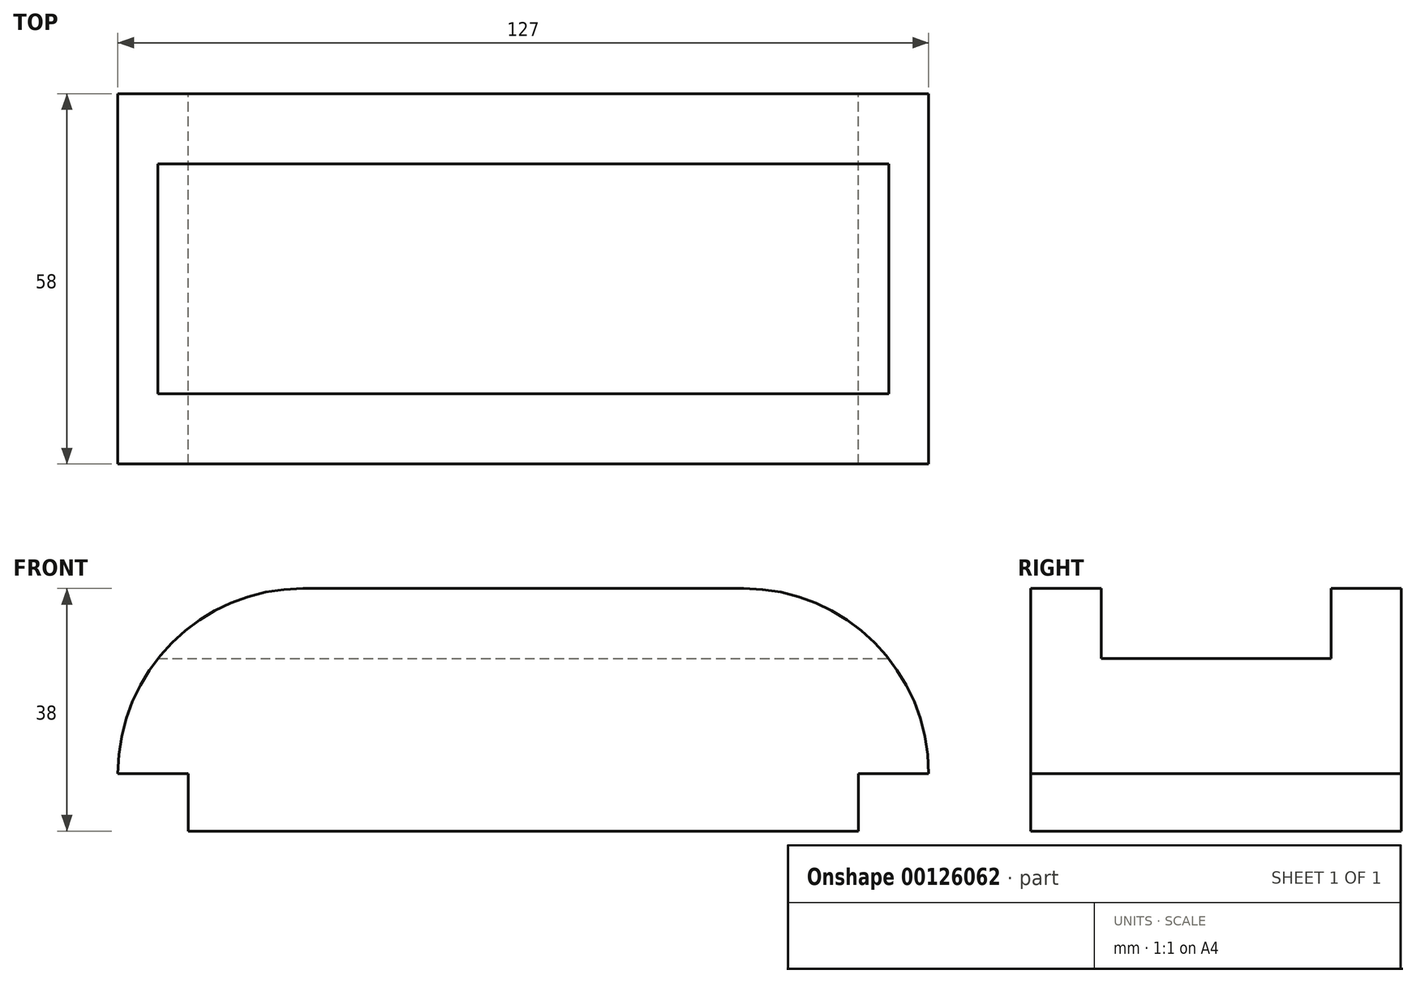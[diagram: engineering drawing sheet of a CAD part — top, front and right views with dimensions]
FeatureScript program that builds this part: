
annotation { "Feature Type Name" : "Feature", "Feature Type Description" : "" }
export const myFeature = defineFeature(function(context is Context, id is Id, definition is map)
    precondition{}
    {
        {
            var Q0;
            Q0=qCreatedBy(makeId("Front.planeOp"),FACE);
            var sketch = newSketch(context, id + "F0", { "sketchPlane" : qUnion([Q0])});
            skLineSegment(sketch, "E0", {"start": v(-52.5, 0) * mm, "end": v(52.5, 0) * mm});
            skLineSegment(sketch, "E1", {"start": v(52.5, 0) * mm, "end": v(52.5, 9) * mm});
            skLineSegment(sketch, "E2", {"start": v(52.5, 9) * mm, "end": v(63.5, 9) * mm});
            skLineSegment(sketch, "E3", {"start": v(-52.5, 0) * mm, "end": v(-52.5, 9) * mm});
            skLineSegment(sketch, "E4", {"start": v(-52.5, 9) * mm, "end": v(-63.5, 9) * mm});
            skLineSegment(sketch, "E5", {"start": v(-63.5, 9) * mm, "end": v(-63.5, 9) * mm});
            skLineSegment(sketch, "E6", {"start": v(-34.5, 38) * mm, "end": v(34.5, 38) * mm});
            skLineSegment(sketch, "E7", {"start": v(63.5, 9) * mm, "end": v(63.5, 9) * mm});
            skPoint(sketch, "E8.visualSharp", {"position": v(-63.5, 38) * mm});
            skArc(sketch, "E8.filletArc", {"start": v(-34.5, 38) * mm, "mid": v(-55, 29.5) * mm, "end": v(-63.5, 9) * mm});
            skPoint(sketch, "E9.visualSharp", {"position": v(63.5, 38) * mm});
            skArc(sketch, "E9.filletArc", {"start": v(63.5, 9) * mm, "mid": v(55, 29.5) * mm, "end": v(34.5, 38) * mm});
            skSolve(sketch);
        }
        {
            var Q0;
            Q0 = qSketchRegion(id + "F0", true);
            extrude(context, id + "F1", {"entities" : qUnion([Q0]), "endBound" : BoundingType.SYMMETRIC, "depth" : 58 * mm});
        }
        {
            var Q0;
            Q0=qCreatedBy(makeId("Right.planeOp"),FACE);
            var sketch = newSketch(context, id + "F2", { "sketchPlane" : qUnion([Q0])});
            skLineSegment(sketch, "E10.bottom", {"start": v(-18, 38) * mm, "end": v(18, 38) * mm});
            skLineSegment(sketch, "E10.top", {"start": v(-18, 27) * mm, "end": v(18, 27) * mm});
            skLineSegment(sketch, "E10.left", {"start": v(-18, 38) * mm, "end": v(-18, 27) * mm});
            skLineSegment(sketch, "E10.right", {"start": v(18, 38) * mm, "end": v(18, 27) * mm});
            skSolve(sketch);
        }
        {
            var Q0;
            Q0 = qSketchRegion(id + "F2", true);
            extrude(context, id + "F3", {"entities" : qUnion([Q0]), "operationType" : NewBodyOperationType.REMOVE, "endBound" : BoundingType.SYMMETRIC, "oppositeDirection" : true, "depth" : 127 * mm});
        }
    });
